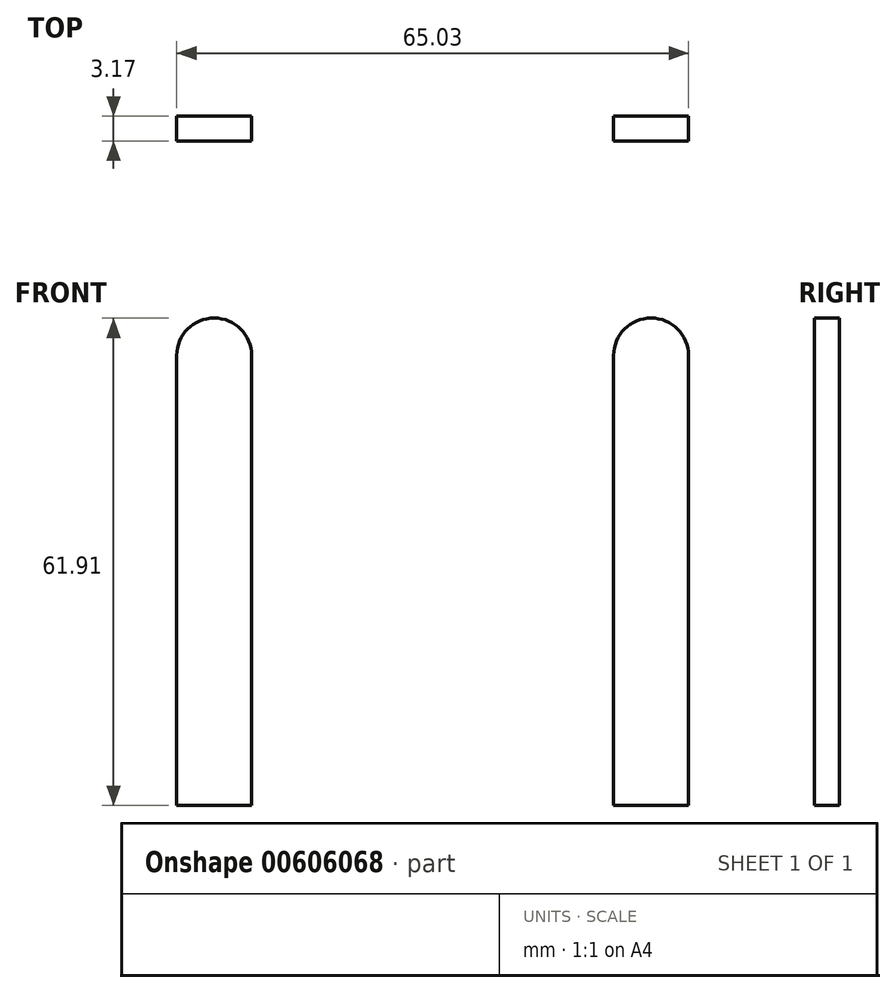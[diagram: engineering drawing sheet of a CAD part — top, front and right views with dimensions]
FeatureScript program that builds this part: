
annotation { "Feature Type Name" : "Feature", "Feature Type Description" : "" }
export const myFeature = defineFeature(function(context is Context, id is Id, definition is map)
    precondition{}
    {
        {
            var Q0;
            Q0=qCreatedBy(makeId("Front.planeOp"),FACE);
            var sketch = newSketch(context, id + "F0", { "sketchPlane" : qUnion([Q0])});
            skLineSegment(sketch, "E0.bottom", {"start": v(0, 0) * mm, "end": v(9.52, 0) * mm});
            skLineSegment(sketch, "E0.top", {"start": v(0, 104.77) * mm, "end": v(9.52, 104.77) * mm});
            skLineSegment(sketch, "E0.left", {"start": v(0, 0) * mm, "end": v(0, 104.77) * mm});
            skLineSegment(sketch, "E0.right", {"start": v(9.53, 0) * mm, "end": v(9.52, 104.77) * mm});
            skArc(sketch, "E1", {"start": v(9.52, 104.77) * mm, "mid": v(4.76, 109.54) * mm, "end": v(0, 104.77) * mm});
            skArc(sketch, "E2", {"start": v(0, 0) * mm, "mid": v(4.76, -4.76) * mm, "end": v(9.53, 0) * mm});
            skLineSegment(sketch, "E3", {"start": v(4.76, 109.54) * mm, "end": v(4.76, -4.76) * mm});
            skLineSegment(sketch, "E4", {"start": v(63.08, 0) * mm, "end": v(63.08, 57.15) * mm});
            skLineSegment(sketch, "E5", {"start": v(63.08, 57.15) * mm, "end": v(72.6, 57.15) * mm});
            skLineSegment(sketch, "E6", {"start": v(72.6, 57.15) * mm, "end": v(72.6, 0) * mm});
            skLineSegment(sketch, "E7", {"start": v(72.6, 0) * mm, "end": v(63.08, 0) * mm});
            skArc(sketch, "E8", {"start": v(72.6, 57.15) * mm, "mid": v(67.85, 61.91) * mm, "end": v(63.08, 57.15) * mm});
            skLineSegment(sketch, "E9", {"start": v(95.6, 58.01) * mm, "end": v(95.6, 0) * mm});
            skLineSegment(sketch, "E10.MirrorCS", {"start": v(128.1, 57.15) * mm, "end": v(118.58, 57.15) * mm});
            skLineSegment(sketch, "E11.MirrorCS", {"start": v(118.58, 0) * mm, "end": v(128.1, 0) * mm});
            skArc(sketch, "E12.MirrorCS", {"start": v(118.58, 57.15) * mm, "mid": v(123.34, 61.91) * mm, "end": v(128.1, 57.15) * mm});
            skLineSegment(sketch, "E13.MirrorCS", {"start": v(118.58, 57.15) * mm, "end": v(118.58, 0) * mm});
            skLineSegment(sketch, "E14.MirrorCS", {"start": v(128.1, 0) * mm, "end": v(128.1, 57.15) * mm});
            skSolve(sketch);
        }
        {
            var Q0;
            Q0=makeQuery(id+"F0.imprint","IMPRINT",FACE,{"disambiguationData":[TD([[makeQuery(id+"F0.imprint","IMPRINT",EDGE,{"derivedFrom":sQuery(id+"F0.wireOp",EDGE,"E4")}),-1.0]])]});
            var Q1;
            Q1=makeQuery(id+"F0.imprint","IMPRINT",FACE,{"disambiguationData":[TD([[makeQuery(id+"F0.imprint","IMPRINT",EDGE,{"derivedFrom":sQuery(id+"F0.wireOp",EDGE,"E5")}),1.0]])]});
            var Q2;
            Q2=makeQuery(id+"F0.imprint","IMPRINT",FACE,{"disambiguationData":[TD([[makeQuery(id+"F0.imprint","IMPRINT",EDGE,{"derivedFrom":sQuery(id+"F0.wireOp",EDGE,"E10.MirrorCS")}),-1.0]])]});
            var Q3;
            Q3=makeQuery(id+"F0.imprint","IMPRINT",FACE,{"disambiguationData":[TD([[makeQuery(id+"F0.imprint","IMPRINT",EDGE,{"derivedFrom":sQuery(id+"F0.wireOp",EDGE,"E10.MirrorCS")}),1.0]])]});
            extrude(context, id + "F1", {"entities" : qUnion([Q0, Q1, Q2, Q3]), "depth" : 3.17 * mm, "offsetDistance" : 25.4 * mm});
        }
    });
